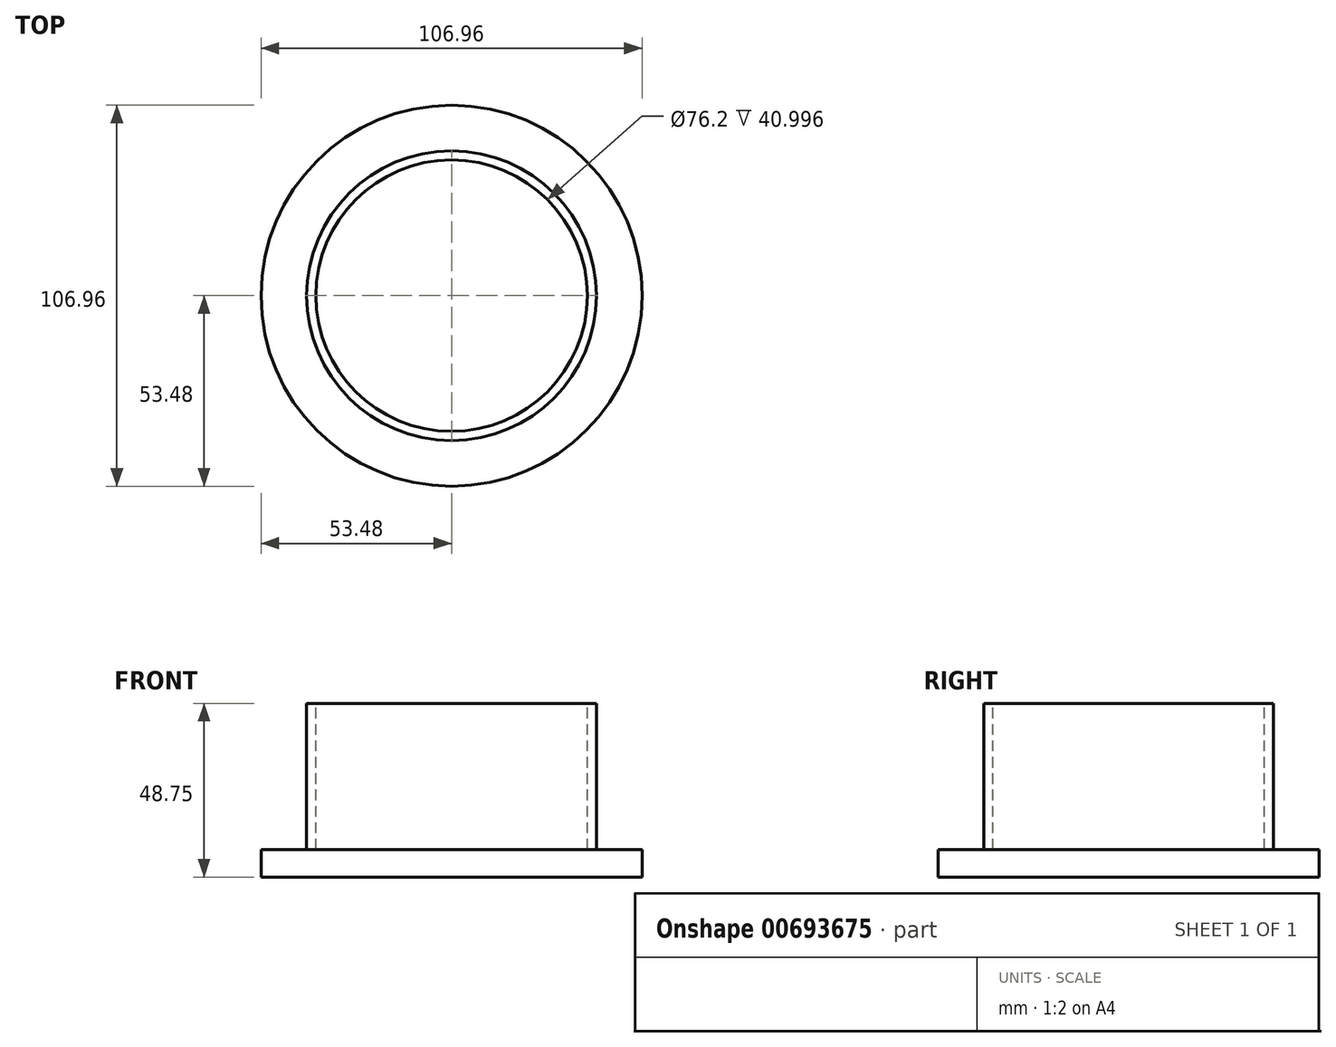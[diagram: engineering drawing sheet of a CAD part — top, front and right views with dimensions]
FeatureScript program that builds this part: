
annotation { "Feature Type Name" : "Feature", "Feature Type Description" : "" }
export const myFeature = defineFeature(function(context is Context, id is Id, definition is map)
    precondition{}
    {
        {
            var Q0;
            Q0=qCreatedBy(makeId("Top.planeOp"),FACE);
            var sketch = newSketch(context, id + "F0", { "sketchPlane" : qUnion([Q0])});
            skCircle(sketch, "E0", {"center": v(0, 0) * mm, "radius": 40.67 * mm});
            skSolve(sketch);
        }
        {
            var Q0;
            Q0=makeQuery(id+"F0.imprint","IMPRINT",FACE,{"disambiguationData":[TD([[makeQuery(id+"F0.imprint","IMPRINT",EDGE,{"derivedFrom":sQuery(id+"F0.wireOp",EDGE,"E0")}),1.0]])]});
            extrude(context, id + "F1", {"entities" : qUnion([Q0]), "depth" : 48.75 * mm, "offsetDistance" : 25.4 * mm});
        }
        {
            var Q0;
            Q0=makeQuery(id+"F1.opExtrude","CAP_FACE",FACE,{"disambiguationData":[OSD([sQuery(id+"F0.wireOp",EDGE,"E0")])],"isStart":false});
            var sketch = newSketch(context, id + "F2", { "sketchPlane" : qUnion([Q0])});
            skCircle(sketch, "E1", {"center": v(0, 0) * mm, "radius": 15.12 * mm});
            skSolve(sketch);
        }
        {
            var Q0;
            Q0=sQuery(id+"F2.wireOp",VERTEX,"E1.center");
            var Q1;
            Q1=makeQuery(id+"F1.opExtrude","SWEPT_BODY",BODY,{"disambiguationData":[OSD([sQuery(id+"F0.wireOp",EDGE,"E0")])]});
            hole(context, id + "F3", {"style" : HoleStyle.SIMPLE, "endStyle" : HoleEndStyle.THROUGH, "holeDiameter" : 76.2 * mm, "majorDiameter" : 6.35 * mm, "isTappedThrough" : true, "tappedDepth" : 12.7 * mm, "tapClearance" : 3, "locations" : qUnion([Q0]), "scope" : qUnion([Q1])});
        }
        {
            var Q0;
            Q0=qCreatedBy(makeId("Top.planeOp"),FACE);
            var sketch = newSketch(context, id + "F4", { "sketchPlane" : qUnion([Q0])});
            skCircle(sketch, "E2", {"center": v(0, 0) * mm, "radius": 53.48 * mm});
            skSolve(sketch);
        }
        {
            var Q0;
            Q0=makeQuery(id+"F4.imprint","IMPRINT",FACE,{"disambiguationData":[TD([[makeQuery(id+"F4.imprint","IMPRINT",EDGE,{"derivedFrom":sQuery(id+"F4.wireOp",EDGE,"E2")}),1.0]])]});
            extrude(context, id + "F5", {"entities" : qUnion([Q0]), "operationType" : NewBodyOperationType.ADD, "depth" : 7.75 * mm, "offsetDistance" : 25.4 * mm});
        }
    });
